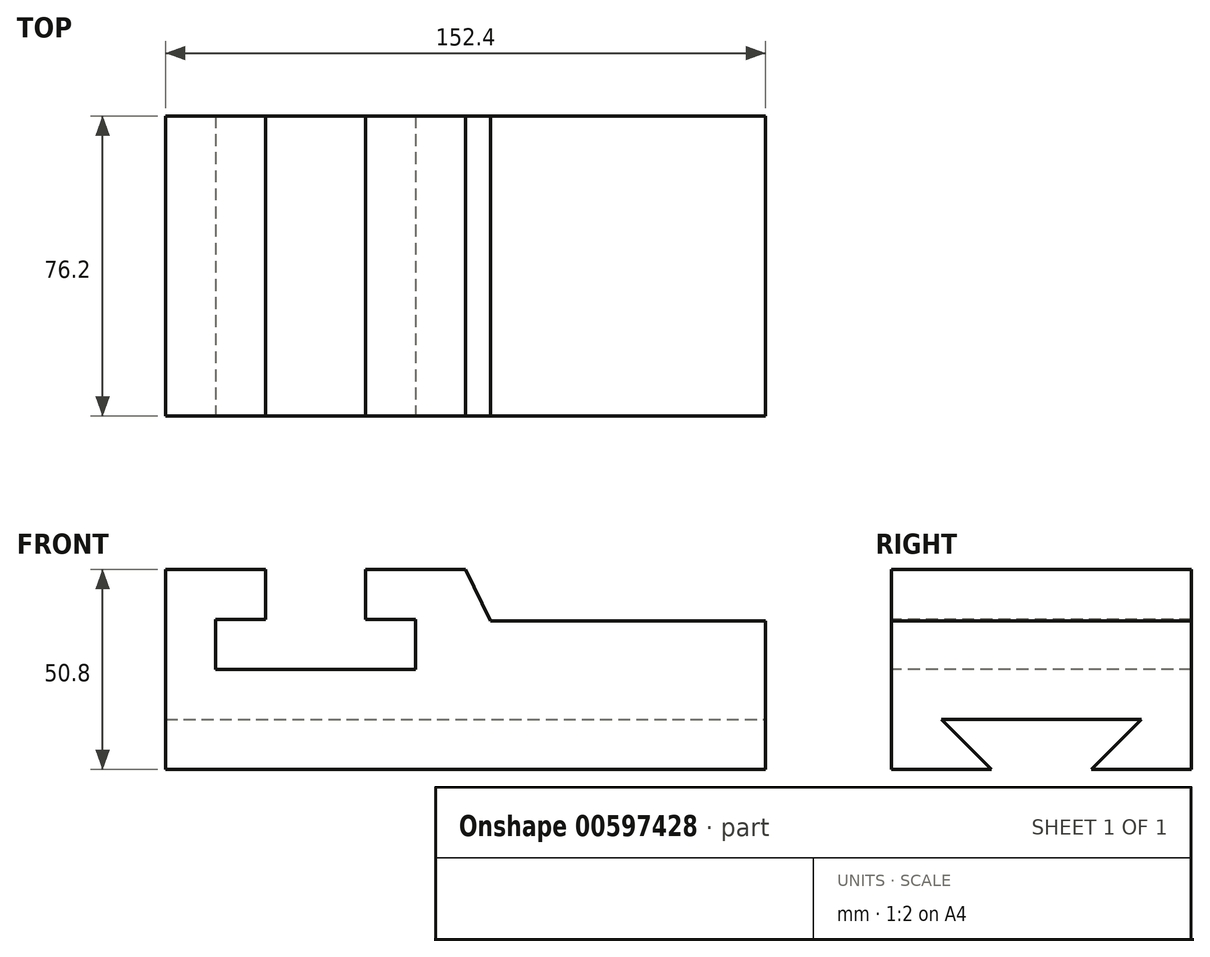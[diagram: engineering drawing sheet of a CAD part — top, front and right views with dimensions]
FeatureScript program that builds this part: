
annotation { "Feature Type Name" : "Feature", "Feature Type Description" : "" }
export const myFeature = defineFeature(function(context is Context, id is Id, definition is map)
    precondition{}
    {
        {
            var Q0;
            Q0=qCreatedBy(makeId("Front.planeOp"),FACE);
            var sketch = newSketch(context, id + "F0", { "sketchPlane" : qUnion([Q0])});
            skLineSegment(sketch, "E0.bottom", {"start": v(0, 0) * mm, "end": v(152.4, 0) * mm});
            skLineSegment(sketch, "E0.top", {"start": v(0, 50.8) * mm, "end": v(152.4, 50.8) * mm});
            skLineSegment(sketch, "E0.left", {"start": v(0, 0) * mm, "end": v(0, 50.8) * mm});
            skLineSegment(sketch, "E0.right", {"start": v(152.4, 0) * mm, "end": v(152.4, 50.8) * mm});
            skSolve(sketch);
        }
        {
            var Q0;
            Q0=makeQuery(id+"F0.imprint","IMPRINT",FACE,{"disambiguationData":[TD([[makeQuery(id+"F0.imprint","IMPRINT",EDGE,{"derivedFrom":sQuery(id+"F0.wireOp",EDGE,"E0.bottom")}),1.0]])]});
            extrude(context, id + "F1", {"entities" : qUnion([Q0]), "oppositeDirection" : true, "depth" : 76.2 * mm, "offsetDistance" : 25.4 * mm});
        }
        {
            var Q0;
            Q0=makeQuery(id+"F1.opExtrude","CAP_FACE",FACE,{"disambiguationData":[OSD([sQuery(id+"F0.wireOp",EDGE,"E0.bottom"),sQuery(id+"F0.wireOp",EDGE,"E0.top"),sQuery(id+"F0.wireOp",EDGE,"E0.left"),sQuery(id+"F0.wireOp",EDGE,"E0.right")])],"isStart":true});
            var sketch = newSketch(context, id + "F2", { "sketchPlane" : qUnion([Q0])});
            skLineSegment(sketch, "E1", {"start": v(0, 0) * mm, "end": v(0, 50.8) * mm});
            skLineSegment(sketch, "E2", {"start": v(0, 50.8) * mm, "end": v(25.4, 50.8) * mm});
            skLineSegment(sketch, "E3", {"start": v(25.4, 50.8) * mm, "end": v(25.4, 38.1) * mm});
            skLineSegment(sketch, "E4", {"start": v(25.4, 38.1) * mm, "end": v(12.7, 38.1) * mm});
            skLineSegment(sketch, "E5", {"start": v(12.7, 38.1) * mm, "end": v(12.7, 25.4) * mm});
            skLineSegment(sketch, "E6", {"start": v(12.7, 25.4) * mm, "end": v(63.5, 25.4) * mm});
            skLineSegment(sketch, "E7", {"start": v(63.5, 25.4) * mm, "end": v(63.5, 38.1) * mm});
            skLineSegment(sketch, "E8", {"start": v(63.5, 38.1) * mm, "end": v(50.8, 38.1) * mm});
            skLineSegment(sketch, "E9", {"start": v(50.8, 38.1) * mm, "end": v(50.8, 50.8) * mm});
            skLineSegment(sketch, "E10", {"start": v(50.8, 50.8) * mm, "end": v(76.2, 50.8) * mm});
            skLineSegment(sketch, "E11", {"start": v(76.2, 50.8) * mm, "end": v(82.55, 37.72) * mm});
            skLineSegment(sketch, "E12", {"start": v(82.55, 37.72) * mm, "end": v(152.4, 37.72) * mm});
            skSolve(sketch);
        }
        {
            var Q0;
            {var subQ0=sQuery(id+"F2.wireOp",EDGE,"E3");Q0=makeQuery(id+"F2.imprint","IMPRINT",FACE,{"disambiguationData":[TD([[makeQuery(id+"F2.imprint","IMPRINT",EDGE,{"derivedFrom":subQ0}),1.0]])]});}
            var Q1;
            {var subQ0=sQuery(id+"F2.wireOp",EDGE,"E11");Q1=makeQuery(id+"F2.imprint","IMPRINT",FACE,{"disambiguationData":[TD([[makeQuery(id+"F2.imprint","IMPRINT",EDGE,{"derivedFrom":subQ0}),1.0]])]});}
            extrude(context, id + "F3", {"entities" : qUnion([Q0, Q1]), "operationType" : NewBodyOperationType.REMOVE, "oppositeDirection" : true, "depth" : 76.2 * mm, "offsetDistance" : 25.4 * mm});
        }
        {
            var Q0;
            Q0=makeQuery(id+"F1.opExtrude","SWEPT_FACE",FACE,{"disambiguationData":[OSD([sQuery(id+"F0.wireOp",EDGE,"E0.right")])]});
            var sketch = newSketch(context, id + "F4", { "sketchPlane" : qUnion([Q0])});
            skLineSegment(sketch, "E13", {"start": v(25.4, 0) * mm, "end": v(12.7, 12.7) * mm});
            skLineSegment(sketch, "E14", {"start": v(12.7, 12.7) * mm, "end": v(63.5, 12.7) * mm});
            skLineSegment(sketch, "E15", {"start": v(63.5, 12.7) * mm, "end": v(50.8, 0) * mm});
            skSolve(sketch);
        }
        {
            var Q0;
            {var subQ0=sQuery(id+"F4.wireOp",EDGE,"E13");Q0=makeQuery(id+"F4.imprint","IMPRINT",FACE,{"disambiguationData":[TD([[makeQuery(id+"F4.imprint","IMPRINT",EDGE,{"derivedFrom":subQ0}),-1.0]])]});}
            extrude(context, id + "F5", {"entities" : qUnion([Q0]), "operationType" : NewBodyOperationType.REMOVE, "oppositeDirection" : true, "depth" : 152.4 * mm, "offsetDistance" : 25.4 * mm});
        }
    });
